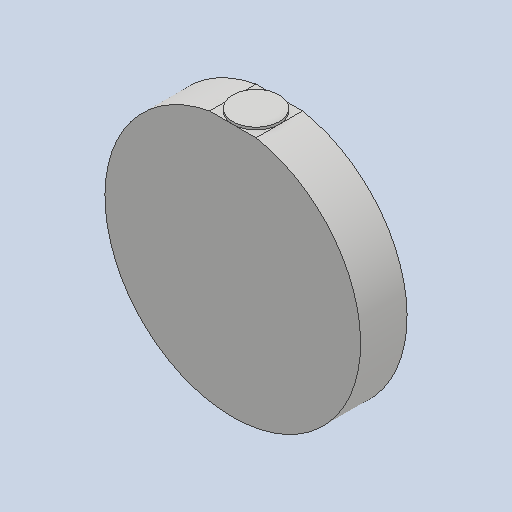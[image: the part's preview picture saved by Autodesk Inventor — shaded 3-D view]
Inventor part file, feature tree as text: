
AUTODESK INVENTOR PART (.ipt)
format: ipt  version: 2024.2 (Build 282272000, 272)  size: 99,840 bytes
history: native  units: mm
features: extrude x2, sketch x2, other x1
ambient origin geometry x8: Origin, YZ Plane, XZ Plane, XY Plane, X Axis, Y Axis, Z Axis, Center Point
bodies: Body1 (feature_tree)
feature tree (5):
  other  "Твердое тело1"
  extrude  "Выдавливание1"  Depth=1.0mm TaperAngle=0.0deg
  extrude  "Выдавливание2"  Depth=55.0mm
  sketch  "Эскиз1"
  sketch  "Эскиз3"
